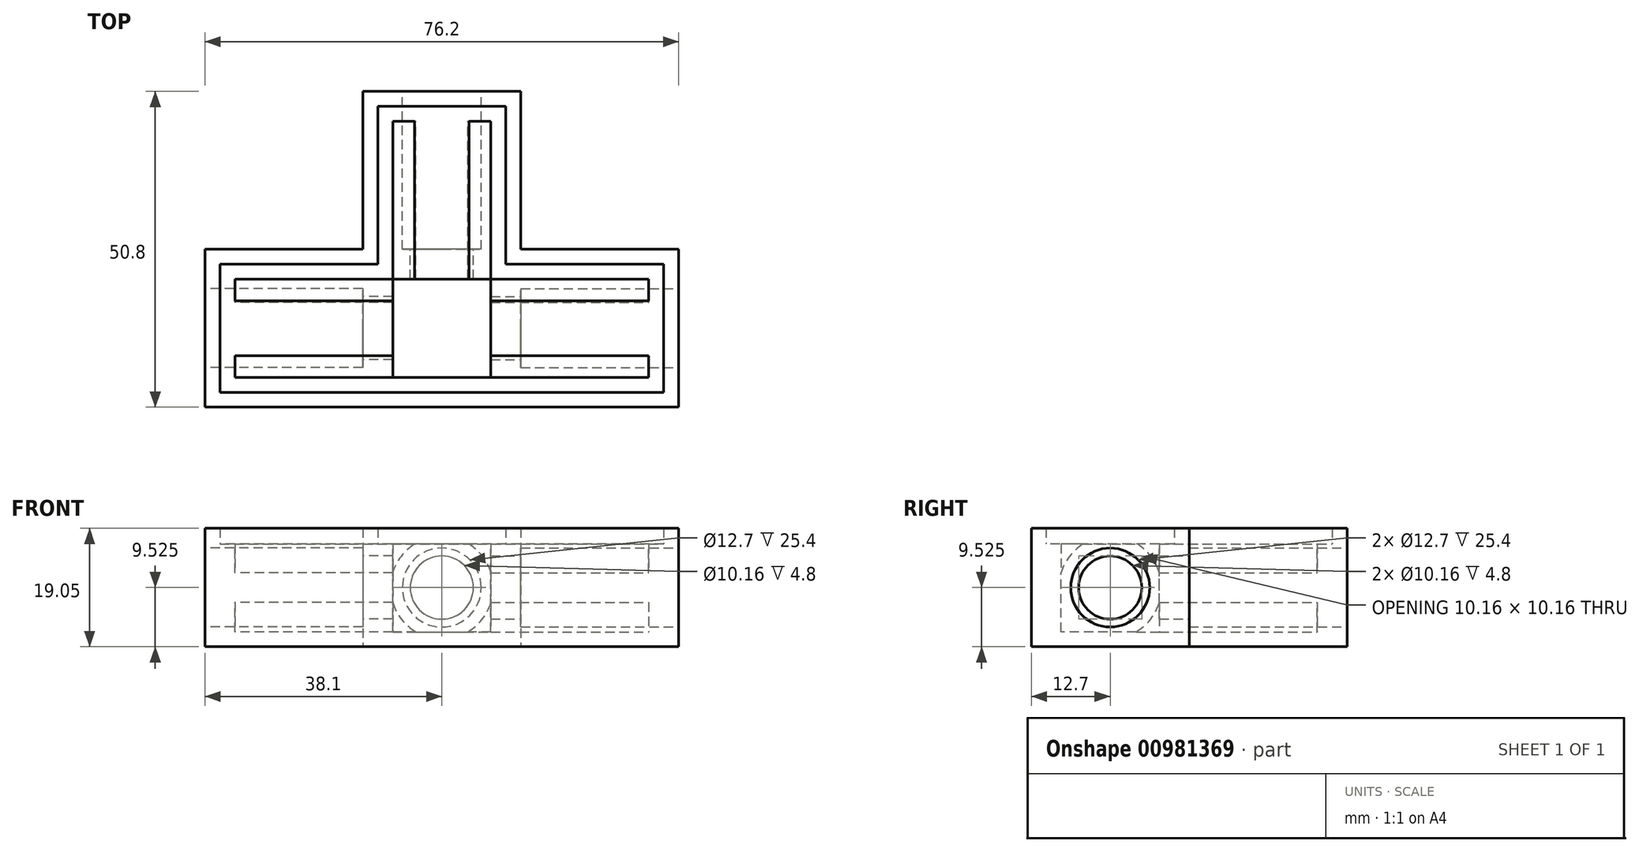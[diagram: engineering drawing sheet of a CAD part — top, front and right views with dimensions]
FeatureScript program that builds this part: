
annotation { "Feature Type Name" : "Feature", "Feature Type Description" : "" }
export const myFeature = defineFeature(function(context is Context, id is Id, definition is map)
    precondition{}
    {
        {
            var Q0;
            Q0=qCreatedBy(makeId("Top.planeOp"),FACE);
            var sketch = newSketch(context, id + "F0", { "sketchPlane" : qUnion([Q0])});
            skLineSegment(sketch, "E0", {"start": v(-38.1, 25.4) * mm, "end": v(-38.1, 0) * mm});
            skLineSegment(sketch, "E1", {"start": v(-38.1, 0) * mm, "end": v(38.1, 0) * mm});
            skLineSegment(sketch, "E2", {"start": v(38.1, 0) * mm, "end": v(38.1, 25.4) * mm});
            skLineSegment(sketch, "E3", {"start": v(38.1, 25.4) * mm, "end": v(12.7, 25.4) * mm});
            skLineSegment(sketch, "E4", {"start": v(12.7, 25.4) * mm, "end": v(12.7, 50.8) * mm});
            skLineSegment(sketch, "E5", {"start": v(12.7, 50.8) * mm, "end": v(-12.7, 50.8) * mm});
            skLineSegment(sketch, "E6", {"start": v(-12.7, 50.8) * mm, "end": v(-12.7, 25.4) * mm});
            skLineSegment(sketch, "E7", {"start": v(-12.7, 25.4) * mm, "end": v(-38.1, 25.4) * mm});
            skSolve(sketch);
        }
        {
            var Q0;
            Q0=makeQuery(id+"F0.imprint","IMPRINT",FACE,{"disambiguationData":[TD([[makeQuery(id+"F0.imprint","IMPRINT",EDGE,{"derivedFrom":sQuery(id+"F0.wireOp",EDGE,"E0")}),1.0]])]});
            extrude(context, id + "F1", {"entities" : qUnion([Q0]), "depth" : 19.05 * mm, "offsetDistance" : 25.4 * mm});
        }
        {
            var Q0;
            Q0=makeQuery(id+"F1.opExtrude","CAP_FACE",FACE,{"disambiguationData":[OSD([sQuery(id+"F0.wireOp",EDGE,"E0"),sQuery(id+"F0.wireOp",EDGE,"E1"),sQuery(id+"F0.wireOp",EDGE,"E2"),sQuery(id+"F0.wireOp",EDGE,"E3"),sQuery(id+"F0.wireOp",EDGE,"E4"),sQuery(id+"F0.wireOp",EDGE,"E5"),sQuery(id+"F0.wireOp",EDGE,"E6"),sQuery(id+"F0.wireOp",EDGE,"E7")])],"isStart":false});
            shell(context, id + "F2", {"entities" : qUnion([Q0]), "thickness" : 2.4 * mm});
        }
        {
            var Q0;
            Q0=makeQuery(id+"F2.opShell","OFFSET_FACE",FACE,{"disambiguationData":[OSD([sQuery(id+"F0.wireOp",EDGE,"E0"),sQuery(id+"F0.wireOp",EDGE,"E1"),sQuery(id+"F0.wireOp",EDGE,"E2"),sQuery(id+"F0.wireOp",EDGE,"E3"),sQuery(id+"F0.wireOp",EDGE,"E4"),sQuery(id+"F0.wireOp",EDGE,"E5"),sQuery(id+"F0.wireOp",EDGE,"E6"),sQuery(id+"F0.wireOp",EDGE,"E7")])]});
            var sketch = newSketch(context, id + "F3", { "sketchPlane" : qUnion([Q0])});
            skLineSegment(sketch, "E8.0", {"start": v(-33.3, 20.6) * mm, "end": v(-33.3, 4.8) * mm});
            skLineSegment(sketch, "E8.1", {"start": v(-7.9, 20.6) * mm, "end": v(-33.3, 20.6) * mm});
            skLineSegment(sketch, "E8.2", {"start": v(-33.3, 4.8) * mm, "end": v(33.3, 4.8) * mm});
            skLineSegment(sketch, "E8.3", {"start": v(-7.9, 46) * mm, "end": v(-7.9, 20.6) * mm});
            skLineSegment(sketch, "E8.4", {"start": v(33.3, 4.8) * mm, "end": v(33.3, 20.6) * mm});
            skLineSegment(sketch, "E8.5", {"start": v(33.3, 20.6) * mm, "end": v(7.9, 20.6) * mm});
            skLineSegment(sketch, "E8.6", {"start": v(7.9, 20.6) * mm, "end": v(7.9, 46) * mm});
            skLineSegment(sketch, "E8.7", {"start": v(7.9, 46) * mm, "end": v(-7.9, 46) * mm});
            skSolve(sketch);
        }
        {
            var Q0;
            Q0=makeQuery(id+"F3.imprint","IMPRINT",FACE,{"disambiguationData":[TD([[makeQuery(id+"F3.imprint","IMPRINT",EDGE,{"derivedFrom":sQuery(id+"F3.wireOp",EDGE,"E8.0")}),-1.0]])]});
            var Q1;
            Q1=makeQuery(id+"F1.opExtrude","CAP_FACE",FACE,{"disambiguationData":[OSD([sQuery(id+"F0.wireOp",EDGE,"E0"),sQuery(id+"F0.wireOp",EDGE,"E1"),sQuery(id+"F0.wireOp",EDGE,"E2"),sQuery(id+"F0.wireOp",EDGE,"E3"),sQuery(id+"F0.wireOp",EDGE,"E4"),sQuery(id+"F0.wireOp",EDGE,"E5"),sQuery(id+"F0.wireOp",EDGE,"E6"),sQuery(id+"F0.wireOp",EDGE,"E7")])],"isStart":false});
            extrude(context, id + "F4", {"entities" : qUnion([Q0]), "operationType" : NewBodyOperationType.ADD, "endBound" : BoundingType.UP_TO_SURFACE, "depth" : 12.95 * mm, "endBoundEntityFace" : qUnion([Q1]), "hasOffset" : true, "offsetDistance" : 2.54 * mm});
        }
        {
            var Q0;
            Q0=makeQuery(id+"F1.opExtrude","SWEPT_FACE",FACE,{"disambiguationData":[OSD([sQuery(id+"F0.wireOp",EDGE,"E5")])]});
            var sketch = newSketch(context, id + "F5", { "sketchPlane" : qUnion([Q0])});
            skCircle(sketch, "E9", {"center": v(0, 9.53) * mm, "radius": 6.35 * mm});
            skCircle(sketch, "E10", {"center": v(0, 9.53) * mm, "radius": 8.26 * mm});
            skCircle(sketch, "E11", {"center": v(0, 9.53) * mm, "radius": 5.08 * mm});
            skSolve(sketch);
        }
        {
            var Q0;
            Q0=makeQuery(id+"F5.imprint","IMPRINT",FACE,{"disambiguationData":[TD([[makeQuery(id+"F5.imprint","IMPRINT",EDGE,{"derivedFrom":sQuery(id+"F5.wireOp",EDGE,"E9")}),-1.0]])]});
            var Q1;
            Q1=makeQuery(id+"F5.imprint","IMPRINT",FACE,{"disambiguationData":[TD([[makeQuery(id+"F5.imprint","IMPRINT",EDGE,{"derivedFrom":sQuery(id+"F5.wireOp",EDGE,"E9")}),1.0]])]});
            var Q2;
            Q2=makeQuery(id+"F5.imprint","IMPRINT",FACE,{"disambiguationData":[TD([[makeQuery(id+"F5.imprint","IMPRINT",EDGE,{"derivedFrom":sQuery(id+"F5.wireOp",EDGE,"E11")}),1.0]])]});
            var Q3;
            Q3=makeQuery(id+"F4.opExtrude","SWEPT_FACE",FACE,{"disambiguationData":[OSD([sQuery(id+"F3.wireOp",EDGE,"E8.1")])]});
            extrude(context, id + "F6", {"entities" : qUnion([Q0, Q1, Q2]), "operationType" : NewBodyOperationType.ADD, "endBound" : BoundingType.UP_TO_SURFACE, "oppositeDirection" : true, "depth" : 30.23 * mm, "endBoundEntityFace" : qUnion([Q3]), "offsetDistance" : 25.4 * mm});
        }
        {
            var Q0;
            Q0=makeQuery(id+"F5.imprint","IMPRINT",FACE,{"disambiguationData":[TD([[makeQuery(id+"F5.imprint","IMPRINT",EDGE,{"derivedFrom":sQuery(id+"F5.wireOp",EDGE,"E9")}),1.0]])]});
            var Q1;
            Q1=makeQuery(id+"F5.imprint","IMPRINT",FACE,{"disambiguationData":[TD([[makeQuery(id+"F5.imprint","IMPRINT",EDGE,{"derivedFrom":sQuery(id+"F5.wireOp",EDGE,"E11")}),1.0]])]});
            extrude(context, id + "F7", {"entities" : qUnion([Q0, Q1]), "operationType" : NewBodyOperationType.REMOVE, "oppositeDirection" : true, "depth" : 25.4 * mm, "offsetDistance" : 25.4 * mm});
        }
        {
            var Q0;
            Q0=makeQuery(id+"F5.imprint","IMPRINT",FACE,{"disambiguationData":[TD([[makeQuery(id+"F5.imprint","IMPRINT",EDGE,{"derivedFrom":sQuery(id+"F5.wireOp",EDGE,"E11")}),1.0]])]});
            extrude(context, id + "F8", {"entities" : qUnion([Q0]), "operationType" : NewBodyOperationType.REMOVE, "oppositeDirection" : true, "depth" : 34.6 * mm, "offsetDistance" : 25.4 * mm});
        }
        {
            var Q0;
            Q0=makeQuery(id+"F1.opExtrude","SWEPT_FACE",FACE,{"disambiguationData":[OSD([sQuery(id+"F0.wireOp",EDGE,"E2")])]});
            var sketch = newSketch(context, id + "F9", { "sketchPlane" : qUnion([Q0])});
            skCircle(sketch, "E12", {"center": v(12.7, 9.53) * mm, "radius": 6.35 * mm});
            skCircle(sketch, "E13", {"center": v(12.7, 9.53) * mm, "radius": 8.26 * mm});
            skCircle(sketch, "E14", {"center": v(12.7, 9.53) * mm, "radius": 5.08 * mm});
            skSolve(sketch);
        }
        {
            var Q0;
            Q0=makeQuery(id+"F9.imprint","IMPRINT",FACE,{"disambiguationData":[TD([[makeQuery(id+"F9.imprint","IMPRINT",EDGE,{"derivedFrom":sQuery(id+"F9.wireOp",EDGE,"E12")}),-1.0]])]});
            var Q1;
            Q1=makeQuery(id+"F9.imprint","IMPRINT",FACE,{"disambiguationData":[TD([[makeQuery(id+"F9.imprint","IMPRINT",EDGE,{"derivedFrom":sQuery(id+"F9.wireOp",EDGE,"E14")}),1.0]])]});
            var Q2;
            Q2=makeQuery(id+"F9.imprint","IMPRINT",FACE,{"disambiguationData":[TD([[makeQuery(id+"F9.imprint","IMPRINT",EDGE,{"derivedFrom":sQuery(id+"F9.wireOp",EDGE,"E12")}),1.0]])]});
            var Q3;
            {var subQ0=sQuery(id+"F3.wireOp",EDGE,"E8.7");var subQ1=sQuery(id+"F3.wireOp",EDGE,"E8.1");var subQ2=sQuery(id+"F3.wireOp",EDGE,"E8.5");var subQ4=sQuery(id+"F3.wireOp",EDGE,"E8.6");Q3=makeQuery(id+"F6.boolean.opBoolean","SPLIT",FACE,{"disambiguationData":[TD([makeQuery(id+"F4.opExtrude","CAP_FACE",FACE,{"disambiguationData":[OSD([sQuery(id+"F0.wireOp",EDGE,"E0"),sQuery(id+"F0.wireOp",EDGE,"E1"),sQuery(id+"F0.wireOp",EDGE,"E2"),sQuery(id+"F0.wireOp",EDGE,"E3"),sQuery(id+"F0.wireOp",EDGE,"E4"),sQuery(id+"F0.wireOp",EDGE,"E5"),sQuery(id+"F0.wireOp",EDGE,"E6"),sQuery(id+"F0.wireOp",EDGE,"E7"),sQuery(id+"F3.wireOp",EDGE,"E8.0"),subQ1,sQuery(id+"F3.wireOp",EDGE,"E8.2"),sQuery(id+"F3.wireOp",EDGE,"E8.3"),sQuery(id+"F3.wireOp",EDGE,"E8.4"),subQ2,subQ4,subQ0])],"isStart":false})])],"derivedFrom":makeQuery(id+"F4.opExtrude","SWEPT_FACE",FACE,{"disambiguationData":[OSD([subQ4])]})});}
            extrude(context, id + "F10", {"entities" : qUnion([Q0, Q1, Q2]), "operationType" : NewBodyOperationType.ADD, "endBound" : BoundingType.UP_TO_SURFACE, "oppositeDirection" : true, "depth" : 25.4 * mm, "endBoundEntityFace" : qUnion([Q3]), "offsetDistance" : 25.4 * mm});
        }
        {
            var Q0;
            Q0=makeQuery(id+"F9.imprint","IMPRINT",FACE,{"disambiguationData":[TD([[makeQuery(id+"F9.imprint","IMPRINT",EDGE,{"derivedFrom":sQuery(id+"F9.wireOp",EDGE,"E12")}),1.0]])]});
            extrude(context, id + "F11", {"entities" : qUnion([Q0]), "operationType" : NewBodyOperationType.REMOVE, "oppositeDirection" : true, "depth" : 25.4 * mm, "offsetDistance" : 25.4 * mm});
        }
        {
            var Q0;
            Q0=makeQuery(id+"F9.imprint","IMPRINT",FACE,{"disambiguationData":[TD([[makeQuery(id+"F9.imprint","IMPRINT",EDGE,{"derivedFrom":sQuery(id+"F9.wireOp",EDGE,"E14")}),1.0]])]});
            extrude(context, id + "F12", {"entities" : qUnion([Q0]), "operationType" : NewBodyOperationType.REMOVE, "oppositeDirection" : true, "depth" : 36.93 * mm, "offsetDistance" : 25.4 * mm});
        }
        {
            var Q0;
            Q0=makeQuery(id+"F1.opExtrude","SWEPT_FACE",FACE,{"disambiguationData":[OSD([sQuery(id+"F0.wireOp",EDGE,"E0")])]});
            var sketch = newSketch(context, id + "F13", { "sketchPlane" : qUnion([Q0])});
            skCircle(sketch, "E15", {"center": v(-12.7, 9.53) * mm, "radius": 6.35 * mm});
            skCircle(sketch, "E16", {"center": v(-12.7, 9.53) * mm, "radius": 5.08 * mm});
            skCircle(sketch, "E17", {"center": v(-12.7, 9.53) * mm, "radius": 8.26 * mm});
            skSolve(sketch);
        }
        {
            var Q0;
            Q0=makeQuery(id+"F13.imprint","IMPRINT",FACE,{"disambiguationData":[TD([[makeQuery(id+"F13.imprint","IMPRINT",EDGE,{"derivedFrom":sQuery(id+"F13.wireOp",EDGE,"E16")}),1.0]])]});
            var Q1;
            Q1=makeQuery(id+"F13.imprint","IMPRINT",FACE,{"disambiguationData":[TD([[makeQuery(id+"F13.imprint","IMPRINT",EDGE,{"derivedFrom":sQuery(id+"F13.wireOp",EDGE,"E15")}),1.0]])]});
            var Q2;
            Q2=makeQuery(id+"F13.imprint","IMPRINT",FACE,{"disambiguationData":[TD([[makeQuery(id+"F13.imprint","IMPRINT",EDGE,{"derivedFrom":sQuery(id+"F13.wireOp",EDGE,"E15")}),-1.0]])]});
            var Q3;
            {var subQ0=sQuery(id+"F3.wireOp",EDGE,"E8.7");var subQ1=sQuery(id+"F3.wireOp",EDGE,"E8.1");var subQ2=sQuery(id+"F3.wireOp",EDGE,"E8.5");var subQ4=sQuery(id+"F3.wireOp",EDGE,"E8.3");Q3=makeQuery(id+"F6.boolean.opBoolean","SPLIT",FACE,{"disambiguationData":[TD([makeQuery(id+"F4.opExtrude","CAP_FACE",FACE,{"disambiguationData":[OSD([sQuery(id+"F0.wireOp",EDGE,"E0"),sQuery(id+"F0.wireOp",EDGE,"E1"),sQuery(id+"F0.wireOp",EDGE,"E2"),sQuery(id+"F0.wireOp",EDGE,"E3"),sQuery(id+"F0.wireOp",EDGE,"E4"),sQuery(id+"F0.wireOp",EDGE,"E5"),sQuery(id+"F0.wireOp",EDGE,"E6"),sQuery(id+"F0.wireOp",EDGE,"E7"),sQuery(id+"F3.wireOp",EDGE,"E8.0"),subQ1,sQuery(id+"F3.wireOp",EDGE,"E8.2"),subQ4,sQuery(id+"F3.wireOp",EDGE,"E8.4"),subQ2,sQuery(id+"F3.wireOp",EDGE,"E8.6"),subQ0])],"isStart":false})])],"derivedFrom":makeQuery(id+"F4.opExtrude","SWEPT_FACE",FACE,{"disambiguationData":[OSD([subQ4])]})});}
            extrude(context, id + "F14", {"entities" : qUnion([Q0, Q1, Q2]), "operationType" : NewBodyOperationType.ADD, "endBound" : BoundingType.UP_TO_SURFACE, "oppositeDirection" : true, "depth" : 25.4 * mm, "endBoundEntityFace" : qUnion([Q3]), "offsetDistance" : 25.4 * mm});
        }
        {
            var Q0;
            Q0=makeQuery(id+"F13.imprint","IMPRINT",FACE,{"disambiguationData":[TD([[makeQuery(id+"F13.imprint","IMPRINT",EDGE,{"derivedFrom":sQuery(id+"F13.wireOp",EDGE,"E15")}),1.0]])]});
            var Q1;
            Q1=makeQuery(id+"F13.imprint","IMPRINT",FACE,{"disambiguationData":[TD([[makeQuery(id+"F13.imprint","IMPRINT",EDGE,{"derivedFrom":sQuery(id+"F13.wireOp",EDGE,"E16")}),1.0]])]});
            extrude(context, id + "F15", {"entities" : qUnion([Q0, Q1]), "operationType" : NewBodyOperationType.REMOVE, "oppositeDirection" : true, "depth" : 25.4 * mm, "offsetDistance" : 25.4 * mm});
        }
        {
            var Q0;
            Q0=makeQuery(id+"F13.imprint","IMPRINT",FACE,{"disambiguationData":[TD([[makeQuery(id+"F13.imprint","IMPRINT",EDGE,{"derivedFrom":sQuery(id+"F13.wireOp",EDGE,"E16")}),1.0]])]});
            extrude(context, id + "F16", {"entities" : qUnion([Q0]), "operationType" : NewBodyOperationType.REMOVE, "oppositeDirection" : true, "depth" : 31.24 * mm, "offsetDistance" : 25.4 * mm});
        }
        {
            var Q0;
            Q0=makeQuery(id+"F2.opShell","OFFSET_FACE",FACE,{"disambiguationData":[OSD([sQuery(id+"F0.wireOp",EDGE,"E0"),sQuery(id+"F0.wireOp",EDGE,"E1"),sQuery(id+"F0.wireOp",EDGE,"E2"),sQuery(id+"F0.wireOp",EDGE,"E3"),sQuery(id+"F0.wireOp",EDGE,"E4"),sQuery(id+"F0.wireOp",EDGE,"E5"),sQuery(id+"F0.wireOp",EDGE,"E6"),sQuery(id+"F0.wireOp",EDGE,"E7")])]});
            var sketch = newSketch(context, id + "F17", { "sketchPlane" : qUnion([Q0])});
            skLineSegment(sketch, "E18.bottom", {"start": v(-7.9, 20.6) * mm, "end": v(7.9, 20.6) * mm});
            skLineSegment(sketch, "E18.top", {"start": v(-7.9, 4.8) * mm, "end": v(7.9, 4.8) * mm});
            skLineSegment(sketch, "E18.left", {"start": v(-7.9, 20.6) * mm, "end": v(-7.9, 4.8) * mm});
            skLineSegment(sketch, "E18.right", {"start": v(7.9, 20.6) * mm, "end": v(7.9, 4.8) * mm});
            skSolve(sketch);
        }
        {
            var Q0;
            {var subQ1=sQuery(id+"F3.wireOp",EDGE,"E8.6");var subQ2=makeQuery(id+"F4.opExtrude","CAP_EDGE",EDGE,{"disambiguationData":[OSD([subQ1])],"isStart":true});Q0=makeQuery(id+"F17.imprint","IMPRINT",FACE,{"disambiguationData":[TD([[makeQuery(id+"F17.imprint","IMPRINT",EDGE,{"derivedFrom":subQ2}),1.0]])]});}
            var Q1;
            {var subQ1=sQuery(id+"F3.wireOp",EDGE,"E8.3");var subQ2=makeQuery(id+"F4.opExtrude","CAP_EDGE",EDGE,{"disambiguationData":[OSD([subQ1])],"isStart":true});Q1=makeQuery(id+"F17.imprint","IMPRINT",FACE,{"disambiguationData":[TD([[makeQuery(id+"F17.imprint","IMPRINT",EDGE,{"derivedFrom":subQ2}),1.0]])]});}
            var Q2;
            {var subQ1=sQuery(id+"F3.wireOp",EDGE,"E8.1");var subQ2=makeQuery(id+"F4.opExtrude","CAP_EDGE",EDGE,{"disambiguationData":[OSD([subQ1])],"isStart":true});Q2=makeQuery(id+"F17.imprint","IMPRINT",FACE,{"disambiguationData":[TD([[makeQuery(id+"F17.imprint","IMPRINT",EDGE,{"derivedFrom":subQ2}),1.0]])]});}
            var Q3;
            {var subQ1=makeQuery(id+"F14.opExtrude","SWEPT_FACE",FACE,{"disambiguationData":[OSD([sQuery(id+"F13.wireOp",EDGE,"E17")])]});var subQ2=makeQuery(id+"F2.opShell","OFFSET_FACE",FACE,{"disambiguationData":[OSD([sQuery(id+"F0.wireOp",EDGE,"E0"),sQuery(id+"F0.wireOp",EDGE,"E1"),sQuery(id+"F0.wireOp",EDGE,"E2"),sQuery(id+"F0.wireOp",EDGE,"E3"),sQuery(id+"F0.wireOp",EDGE,"E4"),sQuery(id+"F0.wireOp",EDGE,"E5"),sQuery(id+"F0.wireOp",EDGE,"E6"),sQuery(id+"F0.wireOp",EDGE,"E7")])]});var subQ3=makeQuery(id+"F14.boolean.opBoolean","INTERSECT",EDGE,{"disambiguationData":[OD(0.0)],"derivedFrom":[subQ2,subQ1]});Q3=makeQuery(id+"F17.imprint","IMPRINT",FACE,{"disambiguationData":[TD([[makeQuery(id+"F17.imprint","IMPRINT",EDGE,{"derivedFrom":subQ3}),-1.0]])]});}
            var Q4;
            {var subQ1=sQuery(id+"F3.wireOp",EDGE,"E8.5");var subQ2=makeQuery(id+"F4.opExtrude","CAP_EDGE",EDGE,{"disambiguationData":[OSD([subQ1])],"isStart":true});Q4=makeQuery(id+"F17.imprint","IMPRINT",FACE,{"disambiguationData":[TD([[makeQuery(id+"F17.imprint","IMPRINT",EDGE,{"derivedFrom":subQ2}),1.0]])]});}
            var Q5;
            {var subQ1=makeQuery(id+"F10.opExtrude","SWEPT_FACE",FACE,{"disambiguationData":[OSD([sQuery(id+"F9.wireOp",EDGE,"E13")])]});var subQ2=makeQuery(id+"F2.opShell","OFFSET_FACE",FACE,{"disambiguationData":[OSD([sQuery(id+"F0.wireOp",EDGE,"E0"),sQuery(id+"F0.wireOp",EDGE,"E1"),sQuery(id+"F0.wireOp",EDGE,"E2"),sQuery(id+"F0.wireOp",EDGE,"E3"),sQuery(id+"F0.wireOp",EDGE,"E4"),sQuery(id+"F0.wireOp",EDGE,"E5"),sQuery(id+"F0.wireOp",EDGE,"E6"),sQuery(id+"F0.wireOp",EDGE,"E7")])]});var subQ3=makeQuery(id+"F10.boolean.opBoolean","INTERSECT",EDGE,{"disambiguationData":[OD(0.0)],"derivedFrom":[subQ2,subQ1]});Q5=makeQuery(id+"F17.imprint","IMPRINT",FACE,{"disambiguationData":[TD([[makeQuery(id+"F17.imprint","IMPRINT",EDGE,{"derivedFrom":subQ3}),-1.0]])]});}
            extrude(context, id + "F18", {"entities" : qUnion([Q0, Q1, Q2, Q3, Q4, Q5]), "operationType" : NewBodyOperationType.ADD, "endBound" : BoundingType.UP_TO_NEXT, "depth" : 25.4 * mm, "offsetDistance" : 25.4 * mm});
        }
        {
            var Q0;
            Q0=makeQuery(id+"F1.opExtrude","CAP_FACE",FACE,{"disambiguationData":[OSD([sQuery(id+"F0.wireOp",EDGE,"E0"),sQuery(id+"F0.wireOp",EDGE,"E1"),sQuery(id+"F0.wireOp",EDGE,"E2"),sQuery(id+"F0.wireOp",EDGE,"E3"),sQuery(id+"F0.wireOp",EDGE,"E4"),sQuery(id+"F0.wireOp",EDGE,"E5"),sQuery(id+"F0.wireOp",EDGE,"E6"),sQuery(id+"F0.wireOp",EDGE,"E7")])],"isStart":false});
            var sketch = newSketch(context, id + "F19", { "sketchPlane" : qUnion([Q0])});
            skLineSegment(sketch, "E19.0", {"start": v(7.9, 20.6) * mm, "end": v(7.9, 46) * mm});
            skPoint(sketch, "E20.0", {"position": v(6.15, 46) * mm});
            skLineSegment(sketch, "E21.0", {"start": v(-4.4, 46) * mm, "end": v(-7.9, 46) * mm});
            skLineSegment(sketch, "E22.0", {"start": v(7.9, 46) * mm, "end": v(4.4, 46) * mm});
            skLineSegment(sketch, "E23.0", {"start": v(-7.9, 46) * mm, "end": v(-7.9, 20.6) * mm});
            skLineSegment(sketch, "E24.0", {"start": v(-7.9, 20.6) * mm, "end": v(-33.3, 20.6) * mm});
            skLineSegment(sketch, "E25.0", {"start": v(33.3, 20.6) * mm, "end": v(7.9, 20.6) * mm});
            skLineSegment(sketch, "E26.0", {"start": v(-33.3, 4.8) * mm, "end": v(33.3, 4.8) * mm});
            skLineSegment(sketch, "E27.0", {"start": v(-33.3, 8.3) * mm, "end": v(-33.3, 4.8) * mm});
            skLineSegment(sketch, "E28.0", {"start": v(-33.3, 20.6) * mm, "end": v(-33.3, 17.1) * mm});
            skLineSegment(sketch, "E29.0", {"start": v(33.3, 17.1) * mm, "end": v(33.3, 20.6) * mm});
            skLineSegment(sketch, "E30.0", {"start": v(33.3, 4.8) * mm, "end": v(33.3, 8.3) * mm});
            skLineSegment(sketch, "E31", {"start": v(-33.3, 20.6) * mm, "end": v(-33.3, 4.8) * mm});
            skLineSegment(sketch, "E32", {"start": v(-7.9, 46) * mm, "end": v(7.9, 46) * mm});
            skLineSegment(sketch, "E33", {"start": v(33.3, 20.6) * mm, "end": v(33.3, 4.8) * mm});
            skPoint(sketch, "E34.0", {"position": v(-7.9, 12.7) * mm});
            skLineSegment(sketch, "E35.0", {"start": v(-7.9, 4.8) * mm, "end": v(-7.9, 20.6) * mm});
            skLineSegment(sketch, "E36.0", {"start": v(-7.9, 20.6) * mm, "end": v(7.9, 20.6) * mm});
            skLineSegment(sketch, "E37.0", {"start": v(7.9, 20.6) * mm, "end": v(7.9, 4.8) * mm});
            skSolve(sketch);
        }
        {
            var Q0;
            {var subQ12=sQuery(id+"F19.wireOp",EDGE,"E19.0");Q0=makeQuery(id+"F19.imprint","IMPRINT",FACE,{"disambiguationData":[TD([[makeQuery(id+"F19.imprint","IMPRINT",EDGE,{"derivedFrom":subQ12}),-1.0]])]});}
            var Q1;
            {var subQ3=sQuery(id+"F19.wireOp",EDGE,"E19.0");Q1=makeQuery(id+"F19.imprint","IMPRINT",FACE,{"disambiguationData":[TD([[makeQuery(id+"F19.imprint","IMPRINT",EDGE,{"derivedFrom":subQ3}),1.0]])]});}
            var Q2;
            {var subQ6=sQuery(id+"F19.wireOp",EDGE,"E24.0");Q2=makeQuery(id+"F19.imprint","IMPRINT",FACE,{"disambiguationData":[TD([[makeQuery(id+"F19.imprint","IMPRINT",EDGE,{"derivedFrom":subQ6}),1.0]])]});}
            var Q3;
            {var subQ3=sQuery(id+"F19.wireOp",EDGE,"E25.0");Q3=makeQuery(id+"F19.imprint","IMPRINT",FACE,{"disambiguationData":[TD([[makeQuery(id+"F19.imprint","IMPRINT",EDGE,{"derivedFrom":subQ3}),1.0]])]});}
            var Q4;
            {var subQ0=sQuery(id+"F3.wireOp",EDGE,"E8.7");var subQ2=sQuery(id+"F3.wireOp",EDGE,"E8.1");var subQ4=sQuery(id+"F0.wireOp",EDGE,"E6");var subQ6=sQuery(id+"F3.wireOp",EDGE,"E8.0");var subQ8=sQuery(id+"F0.wireOp",EDGE,"E0");var subQ9=makeQuery(id+"F2.opShell","OFFSET_FACE",FACE,{"disambiguationData":[OSD([subQ8])]});var subQ12=sQuery(id+"F3.wireOp",EDGE,"E8.3");var subQ14=sQuery(id+"F0.wireOp",EDGE,"E5");var subQ15=makeQuery(id+"F2.opShell","OFFSET_FACE",FACE,{"disambiguationData":[OSD([subQ14])]});var subQ16=sQuery(id+"F3.wireOp",EDGE,"E8.5");var subQ18=sQuery(id+"F0.wireOp",EDGE,"E7");var subQ21=sQuery(id+"F3.wireOp",EDGE,"E8.2");var subQ22=sQuery(id+"F0.wireOp",EDGE,"E1");var subQ23=sQuery(id+"F0.wireOp",EDGE,"E2");var subQ24=sQuery(id+"F3.wireOp",EDGE,"E8.4");Q4=makeQuery(id+"F14.boolean.opBoolean","SPLIT",FACE,{"disambiguationData":[TD([subQ15])],"derivedFrom":makeQuery(id+"F10.boolean.opBoolean","SPLIT",FACE,{"disambiguationData":[TD([subQ9])],"derivedFrom":makeQuery(id+"F4.opExtrude","CAP_FACE",FACE,{"disambiguationData":[OSD([subQ8,subQ22,subQ23,sQuery(id+"F0.wireOp",EDGE,"E3"),sQuery(id+"F0.wireOp",EDGE,"E4"),subQ14,subQ4,subQ18,subQ6,subQ2,subQ21,subQ12,subQ24,subQ16,sQuery(id+"F3.wireOp",EDGE,"E8.6"),subQ0])],"isStart":false})})});}
            extrude(context, id + "F20", {"entities" : qUnion([Q0, Q1, Q2, Q3]), "operationType" : NewBodyOperationType.REMOVE, "endBound" : BoundingType.UP_TO_SURFACE, "oppositeDirection" : true, "depth" : 25.4 * mm, "endBoundEntityFace" : qUnion([Q4]), "offsetDistance" : 25.4 * mm});
        }
    });
